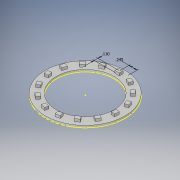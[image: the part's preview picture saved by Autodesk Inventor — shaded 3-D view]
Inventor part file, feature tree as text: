
AUTODESK INVENTOR PART (.ipt)
format: ipt  version: 2017 (Build 210142000, 142)  size: 173,568 bytes
history: native  units: in
note: dims shown in document units (in); Inventor stores cm internally (conversion verified against a paired STEP export)
features: sketch x3, extrude x2, pattern_circular x1
ambient origin geometry x8: Origin, YZ Plane, XZ Plane, XY Plane, X Axis, Y Axis, Z Axis, Center Point
bodies: Solid1 (feature_tree)
feature tree (6):
  extrude  "Extrusion1"  Depth=1.725in
  extrude  "Extrusion2"  Depth=0.13in
  pattern_circular  "Circular Pattern1"  [2 undecoded]
  sketch  "Sketch3"  dims[d5=0.1102in d7=0.0748in d8=0.0in d9=5.9055in d10=360.0deg d12=0.9525in d13=0.245in d14=0.11in]
  sketch  "Sketch1"  dims[d0=2.36in d1=1.725in]
  sketch  "Sketch2"  dims[d2=0.06in d3=0.0in d4=0.13in]
note: 2 required parameter values undecoded (feature->parameter linkage not recoverable at this tier; creation-order binding heuristic only, values carry confidence <= 0.55)
